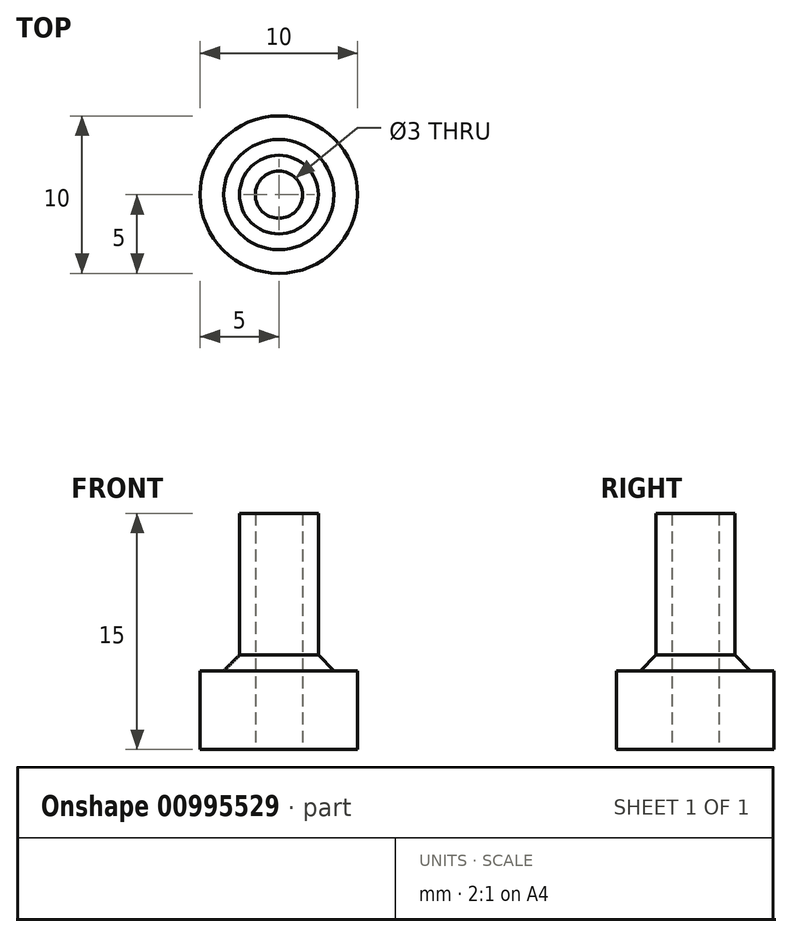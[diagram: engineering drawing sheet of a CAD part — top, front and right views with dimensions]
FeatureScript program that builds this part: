
annotation { "Feature Type Name" : "Feature", "Feature Type Description" : "" }
export const myFeature = defineFeature(function(context is Context, id is Id, definition is map)
    precondition{}
    {
        {
            var Q0;
            Q0=qCreatedBy(makeId("Front.planeOp"),FACE);
            var sketch = newSketch(context, id + "F0", { "sketchPlane" : qUnion([Q0])});
            skLineSegment(sketch, "E0", {"start": v(1.5, 0) * mm, "end": v(1.5, 15) * mm});
            skLineSegment(sketch, "E1", {"start": v(1.5, 15) * mm, "end": v(2.5, 15) * mm});
            skLineSegment(sketch, "E2", {"start": v(2.5, 15) * mm, "end": v(2.5, 6) * mm});
            skLineSegment(sketch, "E3", {"start": v(2.5, 6) * mm, "end": v(3.5, 5) * mm});
            skLineSegment(sketch, "E4", {"start": v(3.5, 5) * mm, "end": v(5, 5) * mm});
            skLineSegment(sketch, "E5", {"start": v(5, 5) * mm, "end": v(5, 0) * mm});
            skLineSegment(sketch, "E6", {"start": v(5, 0) * mm, "end": v(1.5, 0) * mm});
            skLineSegment(sketch, "E7", {"start": v(0, 0) * mm, "end": v(0, 14.89) * mm, "construction": true});
            skSolve(sketch);
        }
        {
            var Q0;
            Q0 = qSketchRegion(id + "F0", true);
            var Q1;
            Q1=sQuery(id+"F0.wireOp",EDGE,"E7");
            revolve(context, id + "F1", {"surfaceOperationType" : NewSurfaceOperationType.NEW, "entities" : qUnion([Q0]), "axis" : qUnion([Q1]), "revolveType" : RevolveType.FULL});
        }
    });
